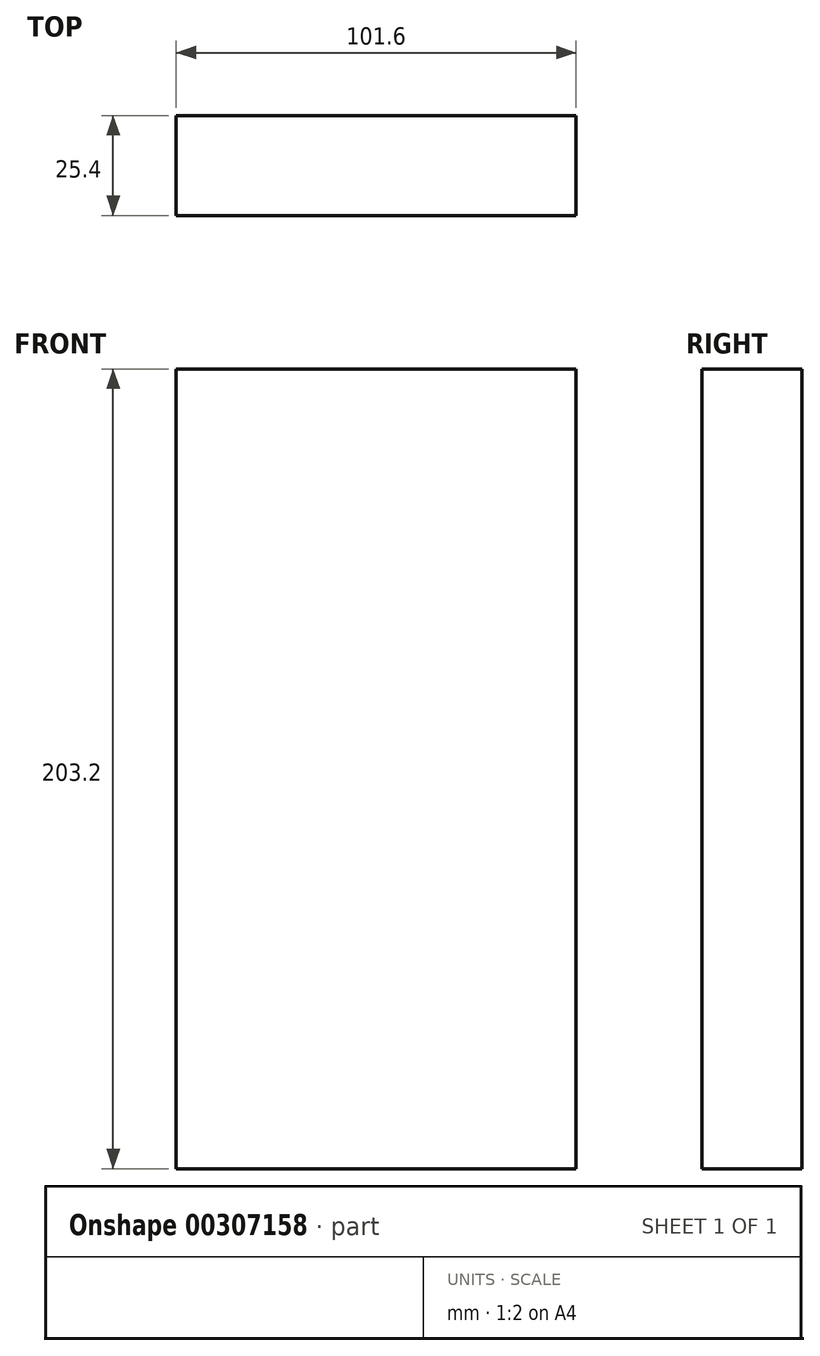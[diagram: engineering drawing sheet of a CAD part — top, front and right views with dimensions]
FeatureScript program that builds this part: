
annotation { "Feature Type Name" : "Feature", "Feature Type Description" : "" }
export const myFeature = defineFeature(function(context is Context, id is Id, definition is map)
    precondition{}
    {
        {
            var Q0;
            Q0=qCreatedBy(makeId("Front.planeOp"),FACE);
            var sketch = newSketch(context, id + "F0", { "sketchPlane" : qUnion([Q0])});
            skLineSegment(sketch, "E0.bottom", {"start": v(-87.74, 116.37) * mm, "end": v(13.86, 116.37) * mm});
            skLineSegment(sketch, "E0.top", {"start": v(-87.74, -86.83) * mm, "end": v(13.86, -86.83) * mm});
            skLineSegment(sketch, "E0.left", {"start": v(-87.74, 116.37) * mm, "end": v(-87.74, -86.83) * mm});
            skLineSegment(sketch, "E0.right", {"start": v(13.86, 116.37) * mm, "end": v(13.86, -86.83) * mm});
            skSolve(sketch);
        }
        {
            var Q0;
            Q0=makeQuery(id+"F0.imprint","IMPRINT",FACE,{"disambiguationData":[TD([[makeQuery(id+"F0.imprint","IMPRINT",EDGE,{"derivedFrom":sQuery(id+"F0.wireOp",EDGE,"E0.bottom")}),-1.0]])]});
            extrude(context, id + "F1", {"entities" : qUnion([Q0]), "depth" : 25.4 * mm});
        }
    });
